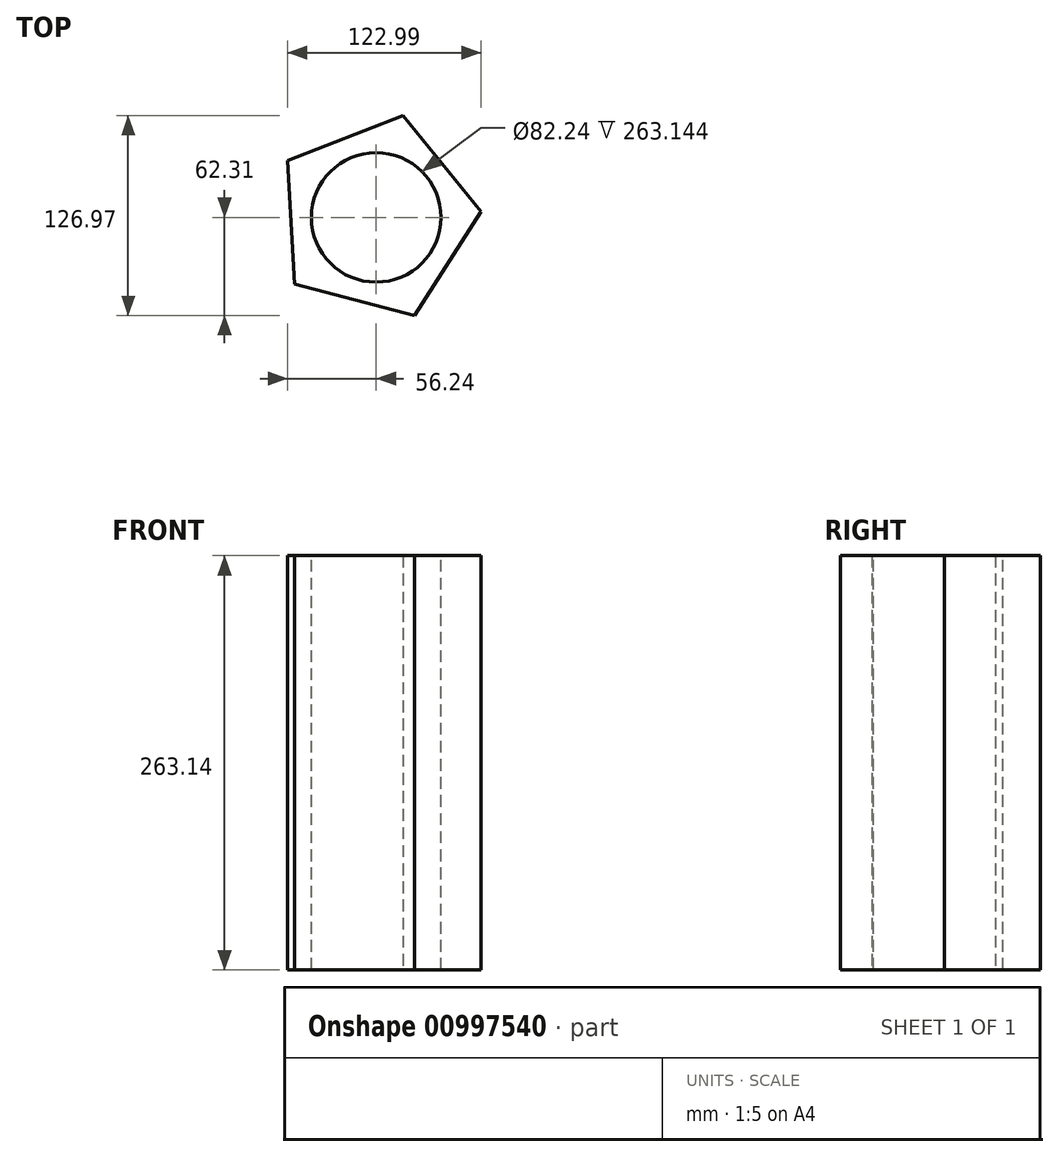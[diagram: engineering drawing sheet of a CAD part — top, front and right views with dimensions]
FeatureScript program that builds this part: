
annotation { "Feature Type Name" : "Feature", "Feature Type Description" : "" }
export const myFeature = defineFeature(function(context is Context, id is Id, definition is map)
    precondition{}
    {
        {
            var Q0;
            Q0=qCreatedBy(makeId("Top.planeOp"),FACE);
            var sketch = newSketch(context, id + "F0", { "sketchPlane" : qUnion([Q0])});
            skLineSegment(sketch, "E0.0", {"start": v(66.75, 3.81) * mm, "end": v(24.25, -62.3) * mm});
            skLineSegment(sketch, "E0.1", {"start": v(24.25, -62.3) * mm, "end": v(-51.76, -42.32) * mm});
            skLineSegment(sketch, "E0.2", {"start": v(-51.76, -42.32) * mm, "end": v(-56.24, 36.15) * mm});
            skLineSegment(sketch, "E0.3", {"start": v(-56.24, 36.15) * mm, "end": v(17, 64.66) * mm});
            skLineSegment(sketch, "E0.4", {"start": v(17, 64.66) * mm, "end": v(66.75, 3.81) * mm});
            skPoint(sketch, "E0.0.midPoint", {"position": v(45.5, -29.25) * mm});
            skSolve(sketch);
        }
        {
            var Q0;
            Q0 = qSketchRegion(id + "F0", true);
            extrude(context, id + "F1", {"entities" : qUnion([Q0]), "depth" : 263.14 * mm, "offsetDistance" : 25.4 * mm});
        }
        {
            var Q0;
            Q0=makeQuery(id+"F1.opExtrude","CAP_FACE",FACE,{"disambiguationData":[OSD([sQuery(id+"F0.wireOp",EDGE,"E0.0"),sQuery(id+"F0.wireOp",EDGE,"E0.1"),sQuery(id+"F0.wireOp",EDGE,"E0.2"),sQuery(id+"F0.wireOp",EDGE,"E0.3"),sQuery(id+"F0.wireOp",EDGE,"E0.4")])],"isStart":false});
            var sketch = newSketch(context, id + "F2", { "sketchPlane" : qUnion([Q0])});
            skCircle(sketch, "E1", {"center": v(0, 0) * mm, "radius": 41.12 * mm});
            skSolve(sketch);
        }
        {
            var Q0;
            Q0=makeQuery(id+"F2.imprint","IMPRINT",FACE,{"disambiguationData":[TD([[makeQuery(id+"F2.imprint","IMPRINT",EDGE,{"derivedFrom":sQuery(id+"F2.wireOp",EDGE,"E1")}),1.0]])]});
            var Q1;
            Q1=sQuery(id+"F2.wireOp",EDGE,"E1");
            extrude(context, id + "F3", {"entities" : qUnion([Q0]), "operationType" : NewBodyOperationType.REMOVE, "surfaceEntities" : qUnion([Q1]), "oppositeDirection" : true, "depth" : 274.57 * mm, "offsetDistance" : 25.4 * mm});
        }
    });
